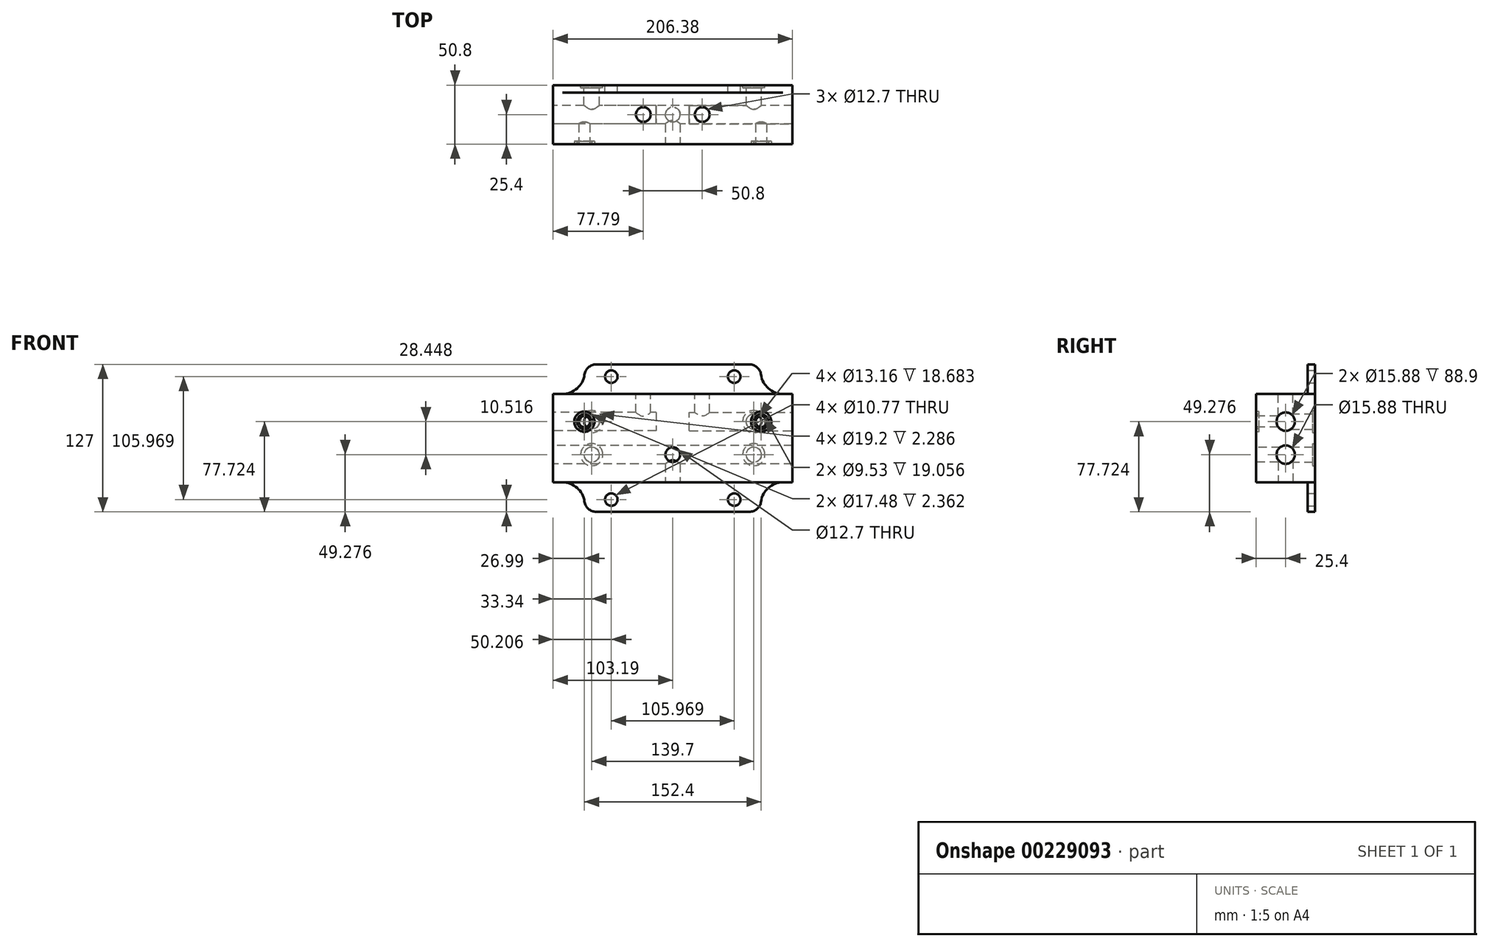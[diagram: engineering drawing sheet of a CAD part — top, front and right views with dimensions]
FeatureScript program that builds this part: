
annotation { "Feature Type Name" : "Feature", "Feature Type Description" : "" }
export const myFeature = defineFeature(function(context is Context, id is Id, definition is map)
    precondition{}
    {
        {
            var Q0;
            Q0=qCreatedBy(makeId("Front.planeOp"),FACE);
            var sketch = newSketch(context, id + "F0", { "sketchPlane" : qUnion([Q0])});
            skLineSegment(sketch, "E0.bottom", {"start": v(-103.19, 38.1) * mm, "end": v(103.19, 38.1) * mm});
            skLineSegment(sketch, "E0.top", {"start": v(-103.19, -38.1) * mm, "end": v(103.19, -38.1) * mm});
            skLineSegment(sketch, "E0.left", {"start": v(-103.19, 38.1) * mm, "end": v(-103.19, -38.1) * mm});
            skLineSegment(sketch, "E0.right", {"start": v(103.19, 38.1) * mm, "end": v(103.19, -38.1) * mm});
            skPoint(sketch, "E0.middle", {"position": v(0, 0) * mm});
            skLineSegment(sketch, "E1", {"start": v(0, 0) * mm, "end": v(0, -14.22) * mm, "construction": true});
            skLineSegment(sketch, "E2", {"start": v(0, -14.22) * mm, "end": v(132.78, -14.22) * mm, "construction": true});
            skLineSegment(sketch, "E3", {"start": v(132.78, -14.22) * mm, "end": v(-138.08, -14.22) * mm, "construction": true});
            skLineSegment(sketch, "E4", {"start": v(-138.08, -14.22) * mm, "end": v(-138.08, 0) * mm, "construction": true});
            skLineSegment(sketch, "E5", {"start": v(-138.08, 0) * mm, "end": v(-138.08, 14.22) * mm, "construction": true});
            skLineSegment(sketch, "E6", {"start": v(-138.08, 14.22) * mm, "end": v(131.45, 14.22) * mm, "construction": true});
            skLineSegment(sketch, "E7", {"start": v(0, -62.52) * mm, "end": v(-50.8, -62.52) * mm, "construction": true});
            skLineSegment(sketch, "E8", {"start": v(-50.8, -62.52) * mm, "end": v(-50.8, -14.22) * mm, "construction": true});
            skLineSegment(sketch, "E9", {"start": v(0, -62.52) * mm, "end": v(50.8, -62.52) * mm, "construction": true});
            skLineSegment(sketch, "E10", {"start": v(50.8, -62.52) * mm, "end": v(50.8, -14.22) * mm, "construction": true});
            skSolve(sketch);
        }
        {
            var Q0;
            Q0=qSketchRegion(id+"F0",true);
            extrude(context, id + "F1", {"entities" : qUnion([Q0]), "oppositeDirection" : true, "depth" : 50.8 * mm});
        }
        {
            var Q0;
            Q0=makeQuery(id+"F1.opExtrude","CAP_FACE",FACE,{"disambiguationData":[OSD([sQuery(id+"F0.wireOp",EDGE,"E0.bottom"),sQuery(id+"F0.wireOp",EDGE,"E0.top"),sQuery(id+"F0.wireOp",EDGE,"E0.left"),sQuery(id+"F0.wireOp",EDGE,"E0.right")])],"isStart":true});
            var sketch = newSketch(context, id + "F2", { "sketchPlane" : qUnion([Q0])});
            skLineSegment(sketch, "E11", {"start": v(125.26, 0) * mm, "end": v(125.26, -14.22) * mm, "construction": true});
            skLineSegment(sketch, "E12", {"start": v(125.26, -14.22) * mm, "end": v(-119.52, -14.22) * mm, "construction": true});
            skLineSegment(sketch, "E13", {"start": v(-119.52, -14.22) * mm, "end": v(-119.52, 0) * mm, "construction": true});
            skLineSegment(sketch, "E14", {"start": v(125.26, 0) * mm, "end": v(125.26, 14.22) * mm, "construction": true});
            skLineSegment(sketch, "E15", {"start": v(125.26, 14.22) * mm, "end": v(-120.4, 14.22) * mm, "construction": true});
            skLineSegment(sketch, "E16", {"start": v(0, 45.29) * mm, "end": v(-76.2, 45.29) * mm, "construction": true});
            skLineSegment(sketch, "E17", {"start": v(-76.2, 45.29) * mm, "end": v(-76.2, -50.15) * mm, "construction": true});
            skLineSegment(sketch, "E18", {"start": v(-76.2, -50.15) * mm, "end": v(76.2, -50.15) * mm, "construction": true});
            skLineSegment(sketch, "E19", {"start": v(76.2, -50.15) * mm, "end": v(76.2, 45.73) * mm, "construction": true});
            skCircle(sketch, "E20", {"center": v(0, -14.22) * mm, "radius": 6.35 * mm});
            skPoint(sketch, "E20.centerSnap0", {"position": v(2.87, -14.22) * mm});
            skLineSegment(sketch, "E21", {"start": v(0, 53.42) * mm, "end": v(25.4, 53.42) * mm, "construction": true});
            skLineSegment(sketch, "E22", {"start": v(25.4, 53.42) * mm, "end": v(25.4, 14.22) * mm, "construction": true});
            skLineSegment(sketch, "E23", {"start": v(25.4, 14.22) * mm, "end": v(76.2, 14.22) * mm, "construction": true});
            skLineSegment(sketch, "E24", {"start": v(76.2, 14.22) * mm, "end": v(76.2, 32.99) * mm, "construction": true});
            skLineSegment(sketch, "E25", {"start": v(0, 53.42) * mm, "end": v(-25.4, 53.42) * mm, "construction": true});
            skLineSegment(sketch, "E26", {"start": v(-25.4, 53.42) * mm, "end": v(-25.4, 14.22) * mm, "construction": true});
            skLineSegment(sketch, "E27", {"start": v(-25.4, 14.22) * mm, "end": v(-76.2, 14.22) * mm, "construction": true});
            skLineSegment(sketch, "E28", {"start": v(-76.2, 14.22) * mm, "end": v(-76.2, 31.87) * mm, "construction": true});
            skCircle(sketch, "E29", {"center": v(-76.2, 14.22) * mm, "radius": 4.76 * mm});
            skCircle(sketch, "E30", {"center": v(76.2, 14.22) * mm, "radius": 4.76 * mm});
            skSolve(sketch);
        }
        {
            var Q0;
            Q0=qSketchRegion(id+"F2",true);
            extrude(context, id + "F3", {"entities" : qUnion([Q0]), "operationType" : NewBodyOperationType.REMOVE, "oppositeDirection" : true, "depth" : 25.4 * mm});
        }
        {
            var Q0;
            Q0=makeQuery(id+"F1.opExtrude","SWEPT_FACE",FACE,{"disambiguationData":[OSD([sQuery(id+"F0.wireOp",EDGE,"E0.left")])]});
            var sketch = newSketch(context, id + "F4", { "sketchPlane" : qUnion([Q0])});
            skLineSegment(sketch, "E31", {"start": v(0, 0) * mm, "end": v(0, -14.22) * mm});
            skLineSegment(sketch, "E32", {"start": v(0, -14.22) * mm, "end": v(-25.4, -14.22) * mm});
            skLineSegment(sketch, "E33", {"start": v(-25.4, -14.22) * mm, "end": v(-25.4, 0) * mm});
            skLineSegment(sketch, "E34", {"start": v(-25.4, 0) * mm, "end": v(-25.4, 14.22) * mm});
            skCircle(sketch, "E35", {"center": v(-25.4, -14.22) * mm, "radius": 7.94 * mm});
            skSolve(sketch);
        }
        {
            var Q0;
            Q0=qSketchRegion(id+"F4",true);
            extrude(context, id + "F5", {"entities" : qUnion([Q0]), "operationType" : NewBodyOperationType.REMOVE, "endBound" : BoundingType.THROUGH_ALL, "oppositeDirection" : true, "depth" : 25.4 * mm});
        }
        {
            var Q0;
            Q0=makeQuery(id+"F1.opExtrude","SWEPT_FACE",FACE,{"disambiguationData":[OSD([sQuery(id+"F0.wireOp",EDGE,"E0.left")])]});
            var sketch = newSketch(context, id + "F6", { "sketchPlane" : qUnion([Q0])});
            skLineSegment(sketch, "E36", {"start": v(0, 0) * mm, "end": v(-25.4, 0) * mm});
            skPoint(sketch, "E36.endSnap0", {"position": v(0, 0) * mm});
            skLineSegment(sketch, "E37", {"start": v(-25.4, 0) * mm, "end": v(-25.4, 14.22) * mm});
            skCircle(sketch, "E38", {"center": v(-25.4, 14.22) * mm, "radius": 7.94 * mm});
            skSolve(sketch);
        }
        {
            var Q0;
            Q0=qSketchRegion(id+"F6",true);
            extrude(context, id + "F7", {"entities" : qUnion([Q0]), "operationType" : NewBodyOperationType.REMOVE, "oppositeDirection" : true, "depth" : 88.9 * mm});
        }
        {
            var Q0;
            Q0=makeQuery(id+"F1.opExtrude","SWEPT_FACE",FACE,{"disambiguationData":[OSD([sQuery(id+"F0.wireOp",EDGE,"E0.right")])]});
            var sketch = newSketch(context, id + "F8", { "sketchPlane" : qUnion([Q0])});
            skLineSegment(sketch, "E39", {"start": v(0, 0) * mm, "end": v(25.4, 0) * mm});
            skLineSegment(sketch, "E40", {"start": v(25.4, 0) * mm, "end": v(25.4, 14.22) * mm});
            skCircle(sketch, "E41", {"center": v(25.4, 14.22) * mm, "radius": 7.94 * mm});
            skSolve(sketch);
        }
        {
            var Q0;
            Q0=qSketchRegion(id+"F8",true);
            extrude(context, id + "F9", {"entities" : qUnion([Q0]), "operationType" : NewBodyOperationType.REMOVE, "oppositeDirection" : true, "depth" : 88.9 * mm});
        }
        {
            var Q0;
            Q0=makeQuery(id+"F1.opExtrude","CAP_FACE",FACE,{"disambiguationData":[OSD([sQuery(id+"F0.wireOp",EDGE,"E0.bottom"),sQuery(id+"F0.wireOp",EDGE,"E0.top"),sQuery(id+"F0.wireOp",EDGE,"E0.left"),sQuery(id+"F0.wireOp",EDGE,"E0.right")])],"isStart":false});
            var sketch = newSketch(context, id + "F10", { "sketchPlane" : qUnion([Q0])});
            skLineSegment(sketch, "E42.bottom", {"start": v(76.2, 63.5) * mm, "end": v(-76.2, 63.5) * mm});
            skLineSegment(sketch, "E42.top", {"start": v(76.2, -63.5) * mm, "end": v(-76.2, -63.5) * mm});
            skLineSegment(sketch, "E42.left", {"start": v(76.2, 63.5) * mm, "end": v(76.2, -63.5) * mm});
            skLineSegment(sketch, "E42.right", {"start": v(-76.2, 63.5) * mm, "end": v(-76.2, -63.5) * mm});
            skPoint(sketch, "E42.middle", {"position": v(0, 0) * mm});
            skSolve(sketch);
        }
        {
            var Q0;
            Q0=qSketchRegion(id+"F10",true);
            extrude(context, id + "F11", {"entities" : qUnion([Q0]), "operationType" : NewBodyOperationType.ADD, "oppositeDirection" : true, "depth" : 6.35 * mm});
        }
        {
            var Q0;
            Q0=makeQuery(id+"F11.opExtrude","SWEPT_EDGE",EDGE,{"disambiguationData":[OSD([sQuery(id+"F10.wireOp",EDGE,"E42.bottom"),sQuery(id+"F10.wireOp",EDGE,"E42.left")])]});
            var Q1;
            Q1=makeQuery(id+"F11.opExtrude","SWEPT_EDGE",EDGE,{"disambiguationData":[OSD([sQuery(id+"F10.wireOp",EDGE,"E42.bottom"),sQuery(id+"F10.wireOp",EDGE,"E42.right")])]});
            var Q2;
            Q2=makeQuery(id+"F11.opExtrude","SWEPT_EDGE",EDGE,{"disambiguationData":[OSD([sQuery(id+"F10.wireOp",EDGE,"E42.top"),sQuery(id+"F10.wireOp",EDGE,"E42.right")])]});
            var Q3;
            Q3=makeQuery(id+"F11.opExtrude","SWEPT_EDGE",EDGE,{"disambiguationData":[OSD([sQuery(id+"F10.wireOp",EDGE,"E42.top"),sQuery(id+"F10.wireOp",EDGE,"E42.left")])]});
            fillet(context, id + "F12", {"entities" : qUnion([Q0, Q1, Q2, Q3]), "radius" : 10.16 * mm, "tangentPropagation" : true, "allowEdgeOverflow" : false});
        }
        {
            var Q0;
            Q0=makeQuery(id+"F11.boolean.opBoolean","INTERSECT",EDGE,{"derivedFrom":[makeQuery(id+"F1.opExtrude","SWEPT_FACE",FACE,{"disambiguationData":[OSD([sQuery(id+"F0.wireOp",EDGE,"E0.top")])]}),makeQuery(id+"F11.opExtrude","SWEPT_FACE",FACE,{"disambiguationData":[OSD([sQuery(id+"F10.wireOp",EDGE,"E42.left")])]})]});
            var Q1;
            Q1=makeQuery(id+"F11.boolean.opBoolean","INTERSECT",EDGE,{"derivedFrom":[makeQuery(id+"F1.opExtrude","SWEPT_FACE",FACE,{"disambiguationData":[OSD([sQuery(id+"F0.wireOp",EDGE,"E0.top")])]}),makeQuery(id+"F11.opExtrude","SWEPT_FACE",FACE,{"disambiguationData":[OSD([sQuery(id+"F10.wireOp",EDGE,"E42.right")])]})]});
            var Q2;
            Q2=makeQuery(id+"F11.boolean.opBoolean","INTERSECT",EDGE,{"derivedFrom":[makeQuery(id+"F1.opExtrude","SWEPT_FACE",FACE,{"disambiguationData":[OSD([sQuery(id+"F0.wireOp",EDGE,"E0.bottom")])]}),makeQuery(id+"F11.opExtrude","SWEPT_FACE",FACE,{"disambiguationData":[OSD([sQuery(id+"F10.wireOp",EDGE,"E42.right")])]})]});
            var Q3;
            Q3=makeQuery(id+"F11.boolean.opBoolean","INTERSECT",EDGE,{"derivedFrom":[makeQuery(id+"F1.opExtrude","SWEPT_FACE",FACE,{"disambiguationData":[OSD([sQuery(id+"F0.wireOp",EDGE,"E0.bottom")])]}),makeQuery(id+"F11.opExtrude","SWEPT_FACE",FACE,{"disambiguationData":[OSD([sQuery(id+"F10.wireOp",EDGE,"E42.left")])]})]});
            fillet(context, id + "F13", {"entities" : qUnion([Q0, Q1, Q2, Q3]), "radius" : 19.05 * mm, "tangentPropagation" : true, "allowEdgeOverflow" : false});
        }
        {
            var Q0;
            Q0=makeQuery(id+"F11.boolean.opBoolean","MERGE",FACE,{"derivedFrom":[makeQuery(id+"F1.opExtrude","CAP_FACE",FACE,{"disambiguationData":[OSD([sQuery(id+"F0.wireOp",EDGE,"E0.bottom"),sQuery(id+"F0.wireOp",EDGE,"E0.top"),sQuery(id+"F0.wireOp",EDGE,"E0.left"),sQuery(id+"F0.wireOp",EDGE,"E0.right")])],"isStart":false}),makeQuery(id+"F11.opExtrude","CAP_FACE",FACE,{"disambiguationData":[OSD([sQuery(id+"F10.wireOp",EDGE,"E42.bottom"),sQuery(id+"F10.wireOp",EDGE,"E42.top"),sQuery(id+"F10.wireOp",EDGE,"E42.left"),sQuery(id+"F10.wireOp",EDGE,"E42.right")])],"isStart":true})]});
            var sketch = newSketch(context, id + "F14", { "sketchPlane" : qUnion([Q0])});
            skPoint(sketch, "E43.middle", {"position": v(0, 0) * mm});
            skCircle(sketch, "E44", {"center": v(-52.98, 52.98) * mm, "radius": 5.38 * mm});
            skCircle(sketch, "E45", {"center": v(52.98, 52.98) * mm, "radius": 5.38 * mm});
            skCircle(sketch, "E46", {"center": v(-52.98, -52.98) * mm, "radius": 5.38 * mm});
            skCircle(sketch, "E47", {"center": v(52.98, -52.98) * mm, "radius": 5.38 * mm});
            skSolve(sketch);
        }
        {
            var Q0;
            Q0=qSketchRegion(id+"F14",true);
            extrude(context, id + "F15", {"entities" : qUnion([Q0]), "operationType" : NewBodyOperationType.REMOVE, "oppositeDirection" : true, "depth" : 25.4 * mm});
        }
        {
            var Q0;
            Q0=makeQuery(id+"F11.boolean.opBoolean","MERGE",FACE,{"derivedFrom":[makeQuery(id+"F1.opExtrude","CAP_FACE",FACE,{"disambiguationData":[OSD([sQuery(id+"F0.wireOp",EDGE,"E0.bottom"),sQuery(id+"F0.wireOp",EDGE,"E0.top"),sQuery(id+"F0.wireOp",EDGE,"E0.left"),sQuery(id+"F0.wireOp",EDGE,"E0.right")])],"isStart":false}),makeQuery(id+"F11.opExtrude","CAP_FACE",FACE,{"disambiguationData":[OSD([sQuery(id+"F10.wireOp",EDGE,"E42.bottom"),sQuery(id+"F10.wireOp",EDGE,"E42.top"),sQuery(id+"F10.wireOp",EDGE,"E42.left"),sQuery(id+"F10.wireOp",EDGE,"E42.right")])],"isStart":true})]});
            var sketch = newSketch(context, id + "F16", { "sketchPlane" : qUnion([Q0])});
            skPoint(sketch, "E48.middle", {"position": v(0, 0) * mm});
            skCircle(sketch, "E49", {"center": v(-69.85, 14.22) * mm, "radius": 6.58 * mm});
            skCircle(sketch, "E50", {"center": v(69.85, 14.22) * mm, "radius": 6.58 * mm});
            skCircle(sketch, "E51", {"center": v(69.85, -14.22) * mm, "radius": 6.58 * mm});
            skCircle(sketch, "E52", {"center": v(-69.85, -14.22) * mm, "radius": 6.58 * mm});
            skSolve(sketch);
        }
        {
            var Q0;
            Q0=qSketchRegion(id+"F16",true);
            extrude(context, id + "F17", {"entities" : qUnion([Q0]), "operationType" : NewBodyOperationType.REMOVE, "oppositeDirection" : true, "depth" : 25.4 * mm});
        }
        {
            var Q0;
            Q0=makeQuery(id+"F1.opExtrude","SWEPT_FACE",FACE,{"disambiguationData":[OSD([sQuery(id+"F0.wireOp",EDGE,"E0.bottom")])]});
            var sketch = newSketch(context, id + "F18", { "sketchPlane" : qUnion([Q0])});
            skPoint(sketch, "E53.endSnap0", {"position": v(0, 0) * mm});
            skCircle(sketch, "E54", {"center": v(25.4, 25.4) * mm, "radius": 6.35 * mm});
            skCircle(sketch, "E55", {"center": v(-25.4, 25.4) * mm, "radius": 6.35 * mm});
            skSolve(sketch);
        }
        {
            var Q0;
            Q0=qSketchRegion(id+"F18",true);
            extrude(context, id + "F19", {"entities" : qUnion([Q0]), "operationType" : NewBodyOperationType.REMOVE, "oppositeDirection" : true, "depth" : 25.4 * mm});
        }
        {
            var Q0;
            Q0=makeQuery(id+"F1.opExtrude","SWEPT_FACE",FACE,{"disambiguationData":[OSD([sQuery(id+"F0.wireOp",EDGE,"E0.top")])]});
            var sketch = newSketch(context, id + "F20", { "sketchPlane" : qUnion([Q0])});
            skPoint(sketch, "E56.endSnap0", {"position": v(0, 0) * mm});
            skCircle(sketch, "E57", {"center": v(0, -25.4) * mm, "radius": 6.35 * mm});
            skSolve(sketch);
        }
        {
            var Q0;
            Q0=qSketchRegion(id+"F20",true);
            extrude(context, id + "F21", {"entities" : qUnion([Q0]), "operationType" : NewBodyOperationType.REMOVE, "oppositeDirection" : true, "depth" : 25.4 * mm});
        }
        {
            var Q0;
            Q0=makeQuery(id+"F11.boolean.opBoolean","MERGE",FACE,{"derivedFrom":[makeQuery(id+"F1.opExtrude","CAP_FACE",FACE,{"disambiguationData":[OSD([sQuery(id+"F0.wireOp",EDGE,"E0.bottom"),sQuery(id+"F0.wireOp",EDGE,"E0.top"),sQuery(id+"F0.wireOp",EDGE,"E0.left"),sQuery(id+"F0.wireOp",EDGE,"E0.right")])],"isStart":false}),makeQuery(id+"F11.opExtrude","CAP_FACE",FACE,{"disambiguationData":[OSD([sQuery(id+"F10.wireOp",EDGE,"E42.bottom"),sQuery(id+"F10.wireOp",EDGE,"E42.top"),sQuery(id+"F10.wireOp",EDGE,"E42.left"),sQuery(id+"F10.wireOp",EDGE,"E42.right")])],"isStart":true})]});
            var sketch = newSketch(context, id + "F22", { "sketchPlane" : qUnion([Q0])});
            skCircle(sketch, "E58", {"center": v(-69.85, 14.22) * mm, "radius": 9.6 * mm});
            skCircle(sketch, "E59", {"center": v(-69.85, -14.22) * mm, "radius": 9.6 * mm});
            skCircle(sketch, "E60", {"center": v(69.85, 14.22) * mm, "radius": 9.6 * mm});
            skCircle(sketch, "E61", {"center": v(69.85, -14.22) * mm, "radius": 9.6 * mm});
            skSolve(sketch);
        }
        {
            var Q0;
            Q0=qSketchRegion(id+"F22",true);
            extrude(context, id + "F23", {"entities" : qUnion([Q0]), "operationType" : NewBodyOperationType.REMOVE, "oppositeDirection" : true, "depth" : 2.3 * mm});
        }
        {
            var Q0;
            Q0=makeQuery(id+"F1.opExtrude","CAP_FACE",FACE,{"disambiguationData":[OSD([sQuery(id+"F0.wireOp",EDGE,"E0.bottom"),sQuery(id+"F0.wireOp",EDGE,"E0.top"),sQuery(id+"F0.wireOp",EDGE,"E0.left"),sQuery(id+"F0.wireOp",EDGE,"E0.right")])],"isStart":true});
            var sketch = newSketch(context, id + "F24", { "sketchPlane" : qUnion([Q0])});
            skCircle(sketch, "E62", {"center": v(76.2, 14.22) * mm, "radius": 8.74 * mm});
            skCircle(sketch, "E63", {"center": v(-76.2, 14.22) * mm, "radius": 8.74 * mm});
            skCircle(sketch, "E64", {"center": v(-76.2, 14.22) * mm, "radius": 6.35 * mm});
            skCircle(sketch, "E65", {"center": v(76.2, 14.22) * mm, "radius": 6.35 * mm});
            skSolve(sketch);
        }
        {
            var Q0;
            Q0=qSketchRegion(id+"F24",true);
            extrude(context, id + "F25", {"entities" : qUnion([Q0]), "operationType" : NewBodyOperationType.REMOVE, "oppositeDirection" : true, "depth" : 2.36 * mm});
        }
    });
